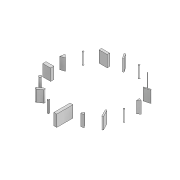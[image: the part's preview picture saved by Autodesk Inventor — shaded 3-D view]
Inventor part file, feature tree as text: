
AUTODESK INVENTOR PART (.ipt)
format: ipt  version: 2021 (Build 250183000, 183)  size: 156,672 bytes
history: native  units: in
note: dims shown in document units (in); Inventor stores cm internally (conversion verified against a paired STEP export)
features: extrude x1, sketch x1
ambient origin geometry x8: Origin, YZ Plane, XZ Plane, XY Plane, X Axis, Y Axis, Z Axis, Center Point
bodies: Solid1 (feature_tree)
feature tree (2):
  extrude  "Extrusion1"  Depth=118.1102in
  sketch  "Sketch1"  dims[d0=787.4016in d1=0.0773in d2=6.2992in d4=360.0deg d6=118.1102in d7=0.0in]
